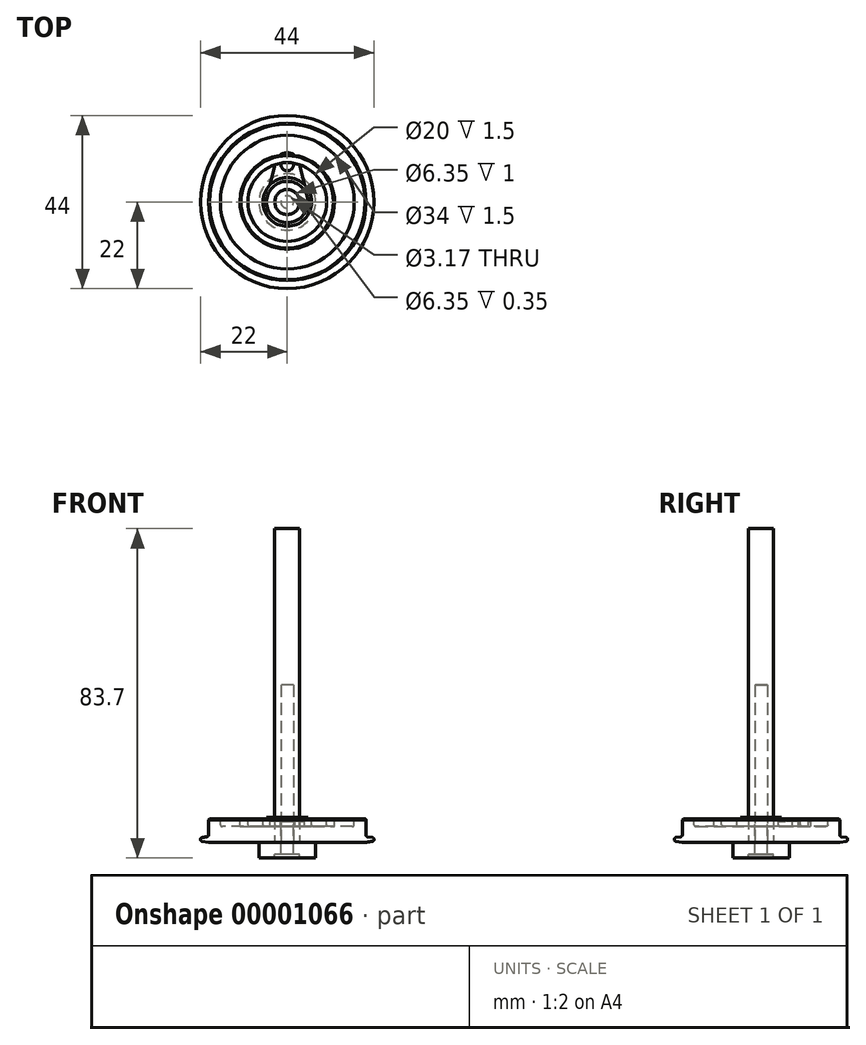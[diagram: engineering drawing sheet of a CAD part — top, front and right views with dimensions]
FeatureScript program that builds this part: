
annotation { "Feature Type Name" : "Feature", "Feature Type Description" : "" }
export const myFeature = defineFeature(function(context is Context, id is Id, definition is map)
    precondition{}
    {
        {
            var Q0;
            Q0=qCreatedBy(makeId("Front.planeOp"),FACE);
            var sketch = newSketch(context, id + "F0", { "sketchPlane" : qUnion([Q0])});
            skLineSegment(sketch, "E0", {"start": v(3.17, 6) * mm, "end": v(6.18, 6) * mm});
            skLineSegment(sketch, "E1", {"start": v(6.18, 6) * mm, "end": v(6.18, 4) * mm});
            skLineSegment(sketch, "E2", {"start": v(6.18, 4) * mm, "end": v(17, 4) * mm});
            skLineSegment(sketch, "E3", {"start": v(17, 4) * mm, "end": v(17, 6) * mm});
            skLineSegment(sketch, "E4", {"start": v(17, 6) * mm, "end": v(20, 6) * mm});
            skLineSegment(sketch, "E5", {"start": v(20, 6) * mm, "end": v(20, 1.5) * mm});
            skLineSegment(sketch, "E6", {"start": v(20, 1.5) * mm, "end": v(22, 1.15) * mm});
            skLineSegment(sketch, "E7", {"start": v(22, 1.15) * mm, "end": v(22, 0.35) * mm});
            skLineSegment(sketch, "E8", {"start": v(22, 0.35) * mm, "end": v(20.03, 0) * mm});
            skLineSegment(sketch, "E9", {"start": v(20.03, 0) * mm, "end": v(7.17, 0) * mm});
            skLineSegment(sketch, "E10", {"start": v(3.17, 0) * mm, "end": v(3.17, 6) * mm});
            skLineSegment(sketch, "E11", {"start": v(0, 5.98) * mm, "end": v(0, 0) * mm, "construction": true});
            skLineSegment(sketch, "E12", {"start": v(3.17, 0) * mm, "end": v(3.17, -4) * mm});
            skLineSegment(sketch, "E13", {"start": v(3.17, -4) * mm, "end": v(7.17, -4) * mm});
            skLineSegment(sketch, "E14", {"start": v(7.17, -4) * mm, "end": v(7.17, 0) * mm});
            skSolve(sketch);
        }
        {
            var Q0;
            Q0=makeQuery(id+"F0.imprint","IMPRINT",FACE,{"disambiguationData":[TD([[makeQuery(id+"F0.imprint","IMPRINT",EDGE,{"derivedFrom":sQuery(id+"F0.wireOp",EDGE,"E0")}),-1.0]])]});
            var Q1;
            Q1=sQuery(id+"F0.wireOp",EDGE,"E11");
            revolve(context, id + "F1", {"entities" : qUnion([Q0]), "axis" : qUnion([Q1]), "revolveType" : RevolveType.FULL});
        }
        {
            var Q0;
            Q0=makeQuery(id+"F1.opRevolve","SWEPT_EDGE",EDGE,{"disambiguationData":[OSD([sQuery(id+"F0.wireOp",EDGE,"E5"),sQuery(id+"F0.wireOp",EDGE,"E6")])]});
            var Q1;
            Q1=makeQuery(id+"F1.opRevolve","SWEPT_EDGE",EDGE,{"disambiguationData":[OSD([sQuery(id+"F0.wireOp",EDGE,"E2"),sQuery(id+"F0.wireOp",EDGE,"E3")])]});
            var Q2;
            Q2=makeQuery(id+"F1.opRevolve","SWEPT_EDGE",EDGE,{"disambiguationData":[OSD([sQuery(id+"F0.wireOp",EDGE,"E1"),sQuery(id+"F0.wireOp",EDGE,"E2")])]});
            fillet(context, id + "F2", {"entities" : qUnion([Q0, Q1, Q2]), "radius" : 0.5 * mm, "allowEdgeOverflow" : false});
        }
        {
            var Q0;
            Q0=makeQuery(id+"F1.opRevolve","SWEPT_EDGE",EDGE,{"disambiguationData":[OSD([sQuery(id+"F0.wireOp",EDGE,"E4"),sQuery(id+"F0.wireOp",EDGE,"E5")])]});
            chamfer(context, id + "F3", {"entities" : qUnion([Q0]), "width" : 0.25 * mm, "tangentPropagation" : true});
        }
        {
            var Q0;
            Q0=makeQuery(id+"F1.opRevolve","SWEPT_FACE",FACE,{"disambiguationData":[OSD([sQuery(id+"F0.wireOp",EDGE,"E7")])]});
            fillet(context, id + "F4", {"entities" : qUnion([Q0]), "radius" : 0.4 * mm, "tangentPropagation" : true, "allowEdgeOverflow" : false});
        }
        {
            var Q0;
            Q0=qCreatedBy(makeId("Top.planeOp"),FACE);
            var sketch = newSketch(context, id + "F5", { "sketchPlane" : qUnion([Q0])});
            skCircle(sketch, "E15", {"center": v(0, 0) * mm, "radius": 3.17 * mm});
            skSolve(sketch);
        }
        {
            var Q0;
            Q0=makeQuery(id+"F5.imprint","IMPRINT",FACE,{"disambiguationData":[TD([[makeQuery(id+"F5.imprint","IMPRINT",EDGE,{"derivedFrom":sQuery(id+"F5.wireOp",EDGE,"E15")}),1.0]])]});
            extrude(context, id + "F6", {"entities" : qUnion([Q0]), "depth" : 79.7 * mm});
        }
        {
            var Q0;
            Q0=qCreatedBy(makeId("Front.planeOp"),FACE);
            var sketch = newSketch(context, id + "F7", { "sketchPlane" : qUnion([Q0])});
            skLineSegment(sketch, "E16", {"start": v(1.59, 6) * mm, "end": v(1.59, 0) * mm});
            skLineSegment(sketch, "E17", {"start": v(4, 0) * mm, "end": v(12, 0) * mm});
            skLineSegment(sketch, "E18", {"start": v(12, 0) * mm, "end": v(14, 0.35) * mm});
            skLineSegment(sketch, "E19", {"start": v(14, 1.15) * mm, "end": v(12, 1.5) * mm});
            skLineSegment(sketch, "E20", {"start": v(12, 1.5) * mm, "end": v(12, 6) * mm});
            skLineSegment(sketch, "E21", {"start": v(12, 6) * mm, "end": v(10, 6) * mm});
            skLineSegment(sketch, "E22", {"start": v(10, 6) * mm, "end": v(10, 4) * mm});
            skLineSegment(sketch, "E23", {"start": v(10, 4) * mm, "end": v(3.59, 4) * mm});
            skLineSegment(sketch, "E24", {"start": v(3.59, 4) * mm, "end": v(3.59, 6) * mm});
            skLineSegment(sketch, "E25", {"start": v(3.59, 6) * mm, "end": v(1.59, 6) * mm});
            skLineSegment(sketch, "E26", {"start": v(14, 0.35) * mm, "end": v(14, 1.15) * mm});
            skLineSegment(sketch, "E27", {"start": v(1.59, -3) * mm, "end": v(1.59, 0) * mm});
            skLineSegment(sketch, "E28", {"start": v(1.59, -3) * mm, "end": v(4, -3) * mm});
            skLineSegment(sketch, "E29", {"start": v(4, -3) * mm, "end": v(4, 0) * mm});
            skLineSegment(sketch, "E30", {"start": v(0, 10) * mm, "end": v(0, -8.7) * mm, "construction": true});
            skSolve(sketch);
        }
        {
            var Q0;
            Q0=makeQuery(id+"F7.imprint","IMPRINT",FACE,{"disambiguationData":[TD([[makeQuery(id+"F7.imprint","IMPRINT",EDGE,{"derivedFrom":sQuery(id+"F7.wireOp",EDGE,"E16")}),1.0]])]});
            var Q1;
            Q1=sQuery(id+"F7.wireOp",EDGE,"E30");
            revolve(context, id + "F8", {"entities" : qUnion([Q0]), "axis" : qUnion([Q1]), "revolveType" : RevolveType.FULL});
        }
        {
            var Q0;
            Q0=makeQuery(id+"F8.opRevolve","SWEPT_EDGE",EDGE,{"disambiguationData":[OSD([sQuery(id+"F7.wireOp",EDGE,"E22"),sQuery(id+"F7.wireOp",EDGE,"E23")])]});
            var Q1;
            Q1=makeQuery(id+"F8.opRevolve","SWEPT_EDGE",EDGE,{"disambiguationData":[OSD([sQuery(id+"F7.wireOp",EDGE,"E23"),sQuery(id+"F7.wireOp",EDGE,"E24")])]});
            var Q2;
            Q2=makeQuery(id+"F8.opRevolve","SWEPT_EDGE",EDGE,{"disambiguationData":[OSD([sQuery(id+"F7.wireOp",EDGE,"E19"),sQuery(id+"F7.wireOp",EDGE,"E20")])]});
            fillet(context, id + "F9", {"entities" : qUnion([Q0, Q1, Q2]), "radius" : 0.5 * mm, "tangentPropagation" : true, "allowEdgeOverflow" : false});
        }
        {
            var Q0;
            Q0=makeQuery(id+"F8.opRevolve","SWEPT_EDGE",EDGE,{"disambiguationData":[OSD([sQuery(id+"F7.wireOp",EDGE,"E19"),sQuery(id+"F7.wireOp",EDGE,"E26")])]});
            var Q1;
            Q1=makeQuery(id+"F8.opRevolve","SWEPT_EDGE",EDGE,{"disambiguationData":[OSD([sQuery(id+"F7.wireOp",EDGE,"E18"),sQuery(id+"F7.wireOp",EDGE,"E26")])]});
            fillet(context, id + "F10", {"entities" : qUnion([Q0, Q1]), "radius" : 0.4 * mm, "tangentPropagation" : true, "allowEdgeOverflow" : false});
        }
        {
            var Q0;
            Q0=makeQuery(id+"F8.opRevolve","SWEPT_EDGE",EDGE,{"disambiguationData":[OSD([sQuery(id+"F7.wireOp",EDGE,"E20"),sQuery(id+"F7.wireOp",EDGE,"E21")])]});
            chamfer(context, id + "F11", {"entities" : qUnion([Q0]), "width" : 0.25 * mm, "tangentPropagation" : true});
        }
        {
            var Q0;
            Q0=qCreatedBy(makeId("Top.planeOp"),FACE);
            var sketch = newSketch(context, id + "F12", { "sketchPlane" : qUnion([Q0])});
            skCircle(sketch, "E31", {"center": v(0, 0) * mm, "radius": 1.59 * mm});
            skSolve(sketch);
        }
        {
            var Q0;
            Q0=makeQuery(id+"F12.imprint","IMPRINT",FACE,{"disambiguationData":[TD([[makeQuery(id+"F12.imprint","IMPRINT",EDGE,{"derivedFrom":sQuery(id+"F12.wireOp",EDGE,"E31")}),1.0]])]});
            extrude(context, id + "F13", {"entities" : qUnion([Q0]), "depth" : 40 * mm});
        }
        {
            var Q0;
            Q0=qCreatedBy(makeId("Top.planeOp"),FACE);
            var sketch = newSketch(context, id + "F14", { "sketchPlane" : qUnion([Q0])});
            skCircle(sketch, "E32", {"center": v(0, 0) * mm, "radius": 5.25 * mm});
            skCircle(sketch, "E33", {"center": v(0, 0) * mm, "radius": 4 * mm});
            skCircle(sketch, "E34", {"center": v(0, 0) * mm, "radius": 3.17 * mm});
            skSolve(sketch);
        }
        {
            var Q0;
            Q0=makeQuery(id+"F14.imprint","IMPRINT",FACE,{"disambiguationData":[TD([[makeQuery(id+"F14.imprint","IMPRINT",EDGE,{"derivedFrom":sQuery(id+"F14.wireOp",EDGE,"E33")}),1.0]])]});
            extrude(context, id + "F15", {"entities" : qUnion([Q0]), "depth" : 4 * mm});
        }
        {
            var Q0;
            Q0=makeQuery(id+"F14.imprint","IMPRINT",FACE,{"disambiguationData":[TD([[makeQuery(id+"F14.imprint","IMPRINT",EDGE,{"derivedFrom":sQuery(id+"F14.wireOp",EDGE,"E32")}),1.0]])]});
            extrude(context, id + "F16", {"entities" : qUnion([Q0]), "operationType" : NewBodyOperationType.ADD, "depth" : 1 * mm});
        }
        {
            var Q0;
            Q0=qCreatedBy(makeId("Top.planeOp"),FACE);
            var sketch = newSketch(context, id + "F17", { "sketchPlane" : qUnion([Q0])});
            skCircle(sketch, "E35", {"center": v(0, 0) * mm, "radius": 3.17 * mm});
            skCircle(sketch, "E36", {"center": v(0, 0) * mm, "radius": 5.25 * mm});
            skCircle(sketch, "E37", {"center": v(0, 9.5) * mm, "radius": 1.59 * mm});
            skArc(sketch, "E38", {"start": v(2.91, 10.21) * mm, "mid": v(0, 12.5) * mm, "end": v(-2.91, 10.21) * mm});
            skLineSegment(sketch, "E39", {"start": v(2.91, 10.21) * mm, "end": v(5.1, 1.24) * mm});
            skLineSegment(sketch, "E40", {"start": v(-2.91, 10.21) * mm, "end": v(-5.1, 1.24) * mm});
            skSolve(sketch);
        }
        {
            var Q0;
            Q0=makeQuery(id+"F17.imprint","IMPRINT",FACE,{"disambiguationData":[TD([[makeQuery(id+"F17.imprint","IMPRINT",EDGE,{"derivedFrom":sQuery(id+"F17.wireOp",EDGE,"E35")}),-1.0]])]});
            extrude(context, id + "F18", {"entities" : qUnion([Q0]), "depth" : 6.35 * mm});
        }
        {
            var Q0;
            Q0=makeQuery(id+"F17.imprint","IMPRINT",FACE,{"disambiguationData":[TD([[makeQuery(id+"F17.imprint","IMPRINT",EDGE,{"derivedFrom":sQuery(id+"F17.wireOp",EDGE,"E37")}),-1.0]])]});
            extrude(context, id + "F19", {"entities" : qUnion([Q0]), "operationType" : NewBodyOperationType.ADD, "depth" : 5.35 * mm});
        }
    });
